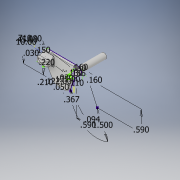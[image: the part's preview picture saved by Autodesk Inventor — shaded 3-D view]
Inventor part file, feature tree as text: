
AUTODESK INVENTOR PART (.ipt)
format: ipt  version: 2018.3 (Build 223284000, 284)  size: 349,696 bytes
history: native  units: in
note: dims shown in document units (in); Inventor stores cm internally (conversion verified against a paired STEP export)
features: extrude x7, sketch x4, fillet x2, revolve x1, plane x1
ambient origin geometry x8: Origin, YZ Plane, XZ Plane, XY Plane, X Axis, Y Axis, Z Axis, Center Point
bodies: Solid1 (feature_tree)
feature tree (15):
  sketch  "Sketch1"  dims[d0=0.1555in d1=0.16in]
  extrude  "Extrusion1"  Depth=0.16in
  extrude  "Extrusion2"  Depth=0.08in
  revolve  "Revolution1"  Angle=135.0deg
  extrude  "Extrusion3"  Depth=0.8383in
  sketch  "Sketch3"  dims[d5=0.71in d6=135.0deg]
  extrude  "Extrusion4"  Depth=0.21in
  extrude  "Extrusion5"  Depth=0.05in
  plane  "Work Plane1"
  extrude  "Extrusion6"  Depth=0.22in
  fillet  "Fillet1"  Radius=0.0687in
  extrude  "Extrusion7"  TaperAngle=45.0deg  [1 undecoded]
  fillet  "Fillet2"  Radius=0.03in
  sketch  "Sketch2"  dims[d2=0.16in d3=0.08in]
  sketch  "Sketch4"  dims[d9=0.367in d10=0.8383in d11=0.21in d12=0.05in d13=0.22in d14=0.0687in d15=45.0deg d16=0.03in d17=0.15in d18=1.5in d19=0.59in d20=0.59in d21=0.094in d22=0.14in d23=0.07in d24=0.0in d25=0.07in d26=0.825in d27=0.0in d28=0.0in d29=0.18in d30=90.0deg d31=0.07in d32=0.307in d33=0.0in d34=0.0in d35=0.03in d36=0.13in d38=0.16in d39=0.11in d40=0.875in d41=0.0in d42=0.57in d43=0.0in d44=0.0in d45=0.54in d46=0.57in d47=0.0in d48=0.0145in d49=0.57in d50=0.0in d51=0.0145in]
note: 1 required parameter value undecoded (feature->parameter linkage not recoverable at this tier; creation-order binding heuristic only, values carry confidence <= 0.55)
